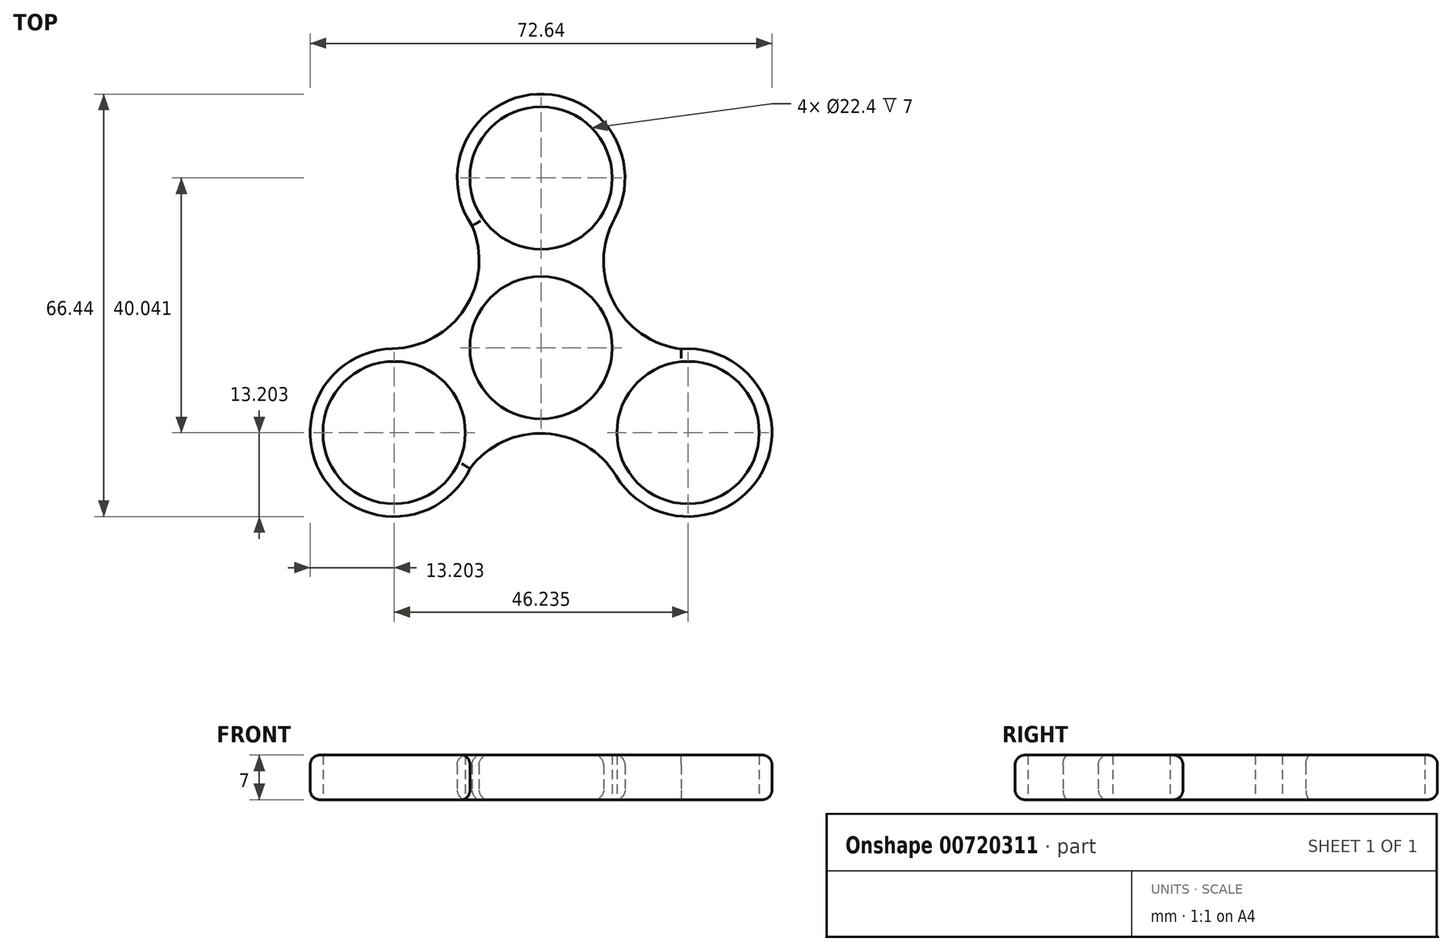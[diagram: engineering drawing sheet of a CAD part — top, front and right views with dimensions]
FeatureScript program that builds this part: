
annotation { "Feature Type Name" : "Feature", "Feature Type Description" : "" }
export const myFeature = defineFeature(function(context is Context, id is Id, definition is map)
    precondition{}
    {
        {
            var Q0;
            Q0=qCreatedBy(makeId("Top.planeOp"),FACE);
            var sketch = newSketch(context, id + "F0", { "sketchPlane" : qUnion([Q0])});
            skCircle(sketch, "E0", {"center": v(0, 0) * mm, "radius": 11.2 * mm});
            skCircle(sketch, "E1", {"center": v(0, 26.7) * mm, "radius": 11.2 * mm});
            skArc(sketch, "E2", {"start": v(11.54, 20.29) * mm, "mid": v(-0.65, 39.88) * mm, "end": v(-10.86, 19.2) * mm});
            skArc(sketch, "E3.1.0", {"start": v(-23.34, -0.15) * mm, "mid": v(-34.21, -20.5) * mm, "end": v(-11.19, -19) * mm});
            skCircle(sketch, "E3.1.1", {"center": v(-23.12, -13.35) * mm, "radius": 11.2 * mm});
            skArc(sketch, "E3.2.0", {"start": v(11.8, -20.14) * mm, "mid": v(34.86, -19.38) * mm, "end": v(22.05, -0.2) * mm});
            skCircle(sketch, "E3.2.1", {"center": v(23.12, -13.35) * mm, "radius": 11.2 * mm});
            skArc(sketch, "E4", {"start": v(11.54, 20.29) * mm, "mid": v(11.36, 7.26) * mm, "end": v(22.05, -0.2) * mm});
            skArc(sketch, "E5.1.0", {"start": v(-23.34, -0.15) * mm, "mid": v(-11.97, 6.2) * mm, "end": v(-10.86, 19.2) * mm});
            skArc(sketch, "E5.2.0", {"start": v(11.8, -20.14) * mm, "mid": v(0.6, -13.47) * mm, "end": v(-11.19, -19) * mm});
            skSolve(sketch);
        }
        {
            var Q0;
            Q0=makeQuery(id+"F0.imprint","IMPRINT",FACE,{"disambiguationData":[TD([[makeQuery(id+"F0.imprint","IMPRINT",EDGE,{"derivedFrom":sQuery(id+"F0.wireOp",EDGE,"E0")}),-1.0]])]});
            extrude(context, id + "F1", {"entities" : qUnion([Q0]), "depth" : 7 * mm, "offsetDistance" : 25 * mm});
        }
        {
            var Q0;
            Q0=makeQuery(id+"F1.opExtrude","CAP_EDGE",EDGE,{"disambiguationData":[OSD([sQuery(id+"F0.wireOp",EDGE,"E5.2.0")])],"isStart":false});
            var Q1;
            Q1=makeQuery(id+"F1.opExtrude","CAP_EDGE",EDGE,{"disambiguationData":[OSD([sQuery(id+"F0.wireOp",EDGE,"E3.1.0")])],"isStart":false});
            var Q2;
            Q2=makeQuery(id+"F1.opExtrude","CAP_EDGE",EDGE,{"disambiguationData":[OSD([sQuery(id+"F0.wireOp",EDGE,"E5.1.0")])],"isStart":false});
            var Q3;
            Q3=makeQuery(id+"F1.opExtrude","CAP_EDGE",EDGE,{"disambiguationData":[OSD([sQuery(id+"F0.wireOp",EDGE,"E2")])],"isStart":false});
            var Q4;
            Q4=makeQuery(id+"F1.opExtrude","CAP_EDGE",EDGE,{"disambiguationData":[OSD([sQuery(id+"F0.wireOp",EDGE,"E4")])],"isStart":false});
            var Q5;
            Q5=makeQuery(id+"F1.opExtrude","CAP_EDGE",EDGE,{"disambiguationData":[OSD([sQuery(id+"F0.wireOp",EDGE,"E3.2.0")])],"isStart":false});
            fillet(context, id + "F2", {"entities" : qUnion([Q0, Q1, Q2, Q3, Q4, Q5]), "radius" : 1.5 * mm, "tangentPropagation" : true, "allowEdgeOverflow" : false});
        }
        {
            var Q0;
            Q0=makeQuery(id+"F1.opExtrude","CAP_EDGE",EDGE,{"disambiguationData":[OSD([sQuery(id+"F0.wireOp",EDGE,"E4")])],"isStart":true});
            var Q1;
            Q1=makeQuery(id+"F1.opExtrude","CAP_EDGE",EDGE,{"disambiguationData":[OSD([sQuery(id+"F0.wireOp",EDGE,"E2")])],"isStart":true});
            var Q2;
            Q2=makeQuery(id+"F1.opExtrude","CAP_EDGE",EDGE,{"disambiguationData":[OSD([sQuery(id+"F0.wireOp",EDGE,"E5.1.0")])],"isStart":true});
            var Q3;
            Q3=makeQuery(id+"F1.opExtrude","CAP_EDGE",EDGE,{"disambiguationData":[OSD([sQuery(id+"F0.wireOp",EDGE,"E3.1.0")])],"isStart":true});
            var Q4;
            Q4=makeQuery(id+"F1.opExtrude","CAP_EDGE",EDGE,{"disambiguationData":[OSD([sQuery(id+"F0.wireOp",EDGE,"E5.2.0")])],"isStart":true});
            var Q5;
            Q5=makeQuery(id+"F1.opExtrude","CAP_EDGE",EDGE,{"disambiguationData":[OSD([sQuery(id+"F0.wireOp",EDGE,"E3.2.0")])],"isStart":true});
            fillet(context, id + "F3", {"entities" : qUnion([Q0, Q1, Q2, Q3, Q4, Q5]), "radius" : 1.5 * mm, "tangentPropagation" : true, "allowEdgeOverflow" : false});
        }
    });
